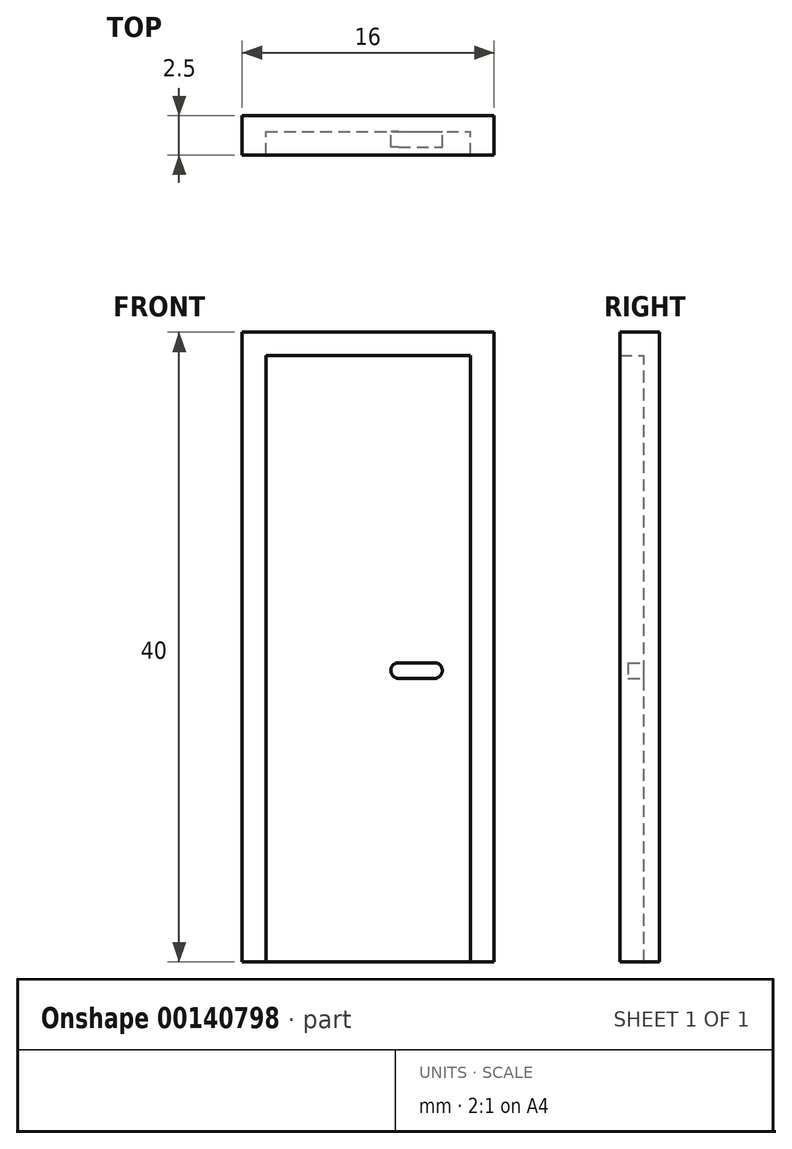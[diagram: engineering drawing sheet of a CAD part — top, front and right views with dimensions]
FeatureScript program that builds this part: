
annotation { "Feature Type Name" : "Feature", "Feature Type Description" : "" }
export const myFeature = defineFeature(function(context is Context, id is Id, definition is map)
    precondition{}
    {
        {
            var Q0;
            Q0=qCreatedBy(makeId("Front.planeOp"),FACE);
            var sketch = newSketch(context, id + "F0", { "sketchPlane" : qUnion([Q0])});
            skLineSegment(sketch, "E0.bottom", {"start": v(-11.07, 0) * mm, "end": v(4.93, 0) * mm});
            skLineSegment(sketch, "E0.top", {"start": v(-11.07, 40) * mm, "end": v(4.93, 40) * mm});
            skLineSegment(sketch, "E0.left", {"start": v(-11.07, 0) * mm, "end": v(-11.07, 40) * mm});
            skLineSegment(sketch, "E0.right", {"start": v(4.93, 0) * mm, "end": v(4.93, 40) * mm});
            skLineSegment(sketch, "E1.0", {"start": v(3.43, 0) * mm, "end": v(3.43, 38.5) * mm});
            skLineSegment(sketch, "E1.1", {"start": v(-9.57, 38.5) * mm, "end": v(3.43, 38.5) * mm});
            skLineSegment(sketch, "E1.2", {"start": v(-9.57, 0) * mm, "end": v(-9.57, 38.5) * mm});
            skSolve(sketch);
        }
        {
            var Q0;
            Q0=makeQuery(id+"F0.imprint","IMPRINT",FACE,{"disambiguationData":[TD([[makeQuery(id+"F0.imprint","IMPRINT",EDGE,{"derivedFrom":sQuery(id+"F0.wireOp",EDGE,"E0.top")}),-1.0]])]});
            extrude(context, id + "F1", {"entities" : qUnion([Q0]), "depth" : 2.5 * mm});
        }
        {
            var Q0;
            {var subQ0=sQuery(id+"F0.wireOp",EDGE,"E1.0");Q0=makeQuery(id+"F0.imprint","IMPRINT",FACE,{"disambiguationData":[TD([[makeQuery(id+"F0.imprint","IMPRINT",EDGE,{"derivedFrom":subQ0}),1.0]])]});}
            extrude(context, id + "F2", {"entities" : qUnion([Q0]), "operationType" : NewBodyOperationType.ADD, "depth" : 1 * mm});
        }
        {
            var Q0;
            Q0=makeQuery(id+"F2.opExtrude","CAP_FACE",FACE,{"disambiguationData":[OSD([sQuery(id+"F0.wireOp",EDGE,"E0.bottom"),sQuery(id+"F0.wireOp",EDGE,"E1.0"),sQuery(id+"F0.wireOp",EDGE,"E1.1"),sQuery(id+"F0.wireOp",EDGE,"E1.2")])],"isStart":false});
            var sketch = newSketch(context, id + "F3", { "sketchPlane" : qUnion([Q0])});
            skLineSegment(sketch, "E2", {"start": v(-1.13, 19) * mm, "end": v(1.14, 19) * mm});
            skLineSegment(sketch, "E3.0", {"start": v(-1.13, 18) * mm, "end": v(1.14, 18) * mm});
            skArc(sketch, "E4", {"start": v(-1.13, 19) * mm, "mid": v(-1.63, 18.5) * mm, "end": v(-1.13, 18) * mm});
            skArc(sketch, "E5", {"start": v(1.14, 18) * mm, "mid": v(1.64, 18.5) * mm, "end": v(1.14, 19) * mm});
            skSolve(sketch);
        }
        {
            var Q0;
            Q0=makeQuery(id+"F3.imprint","IMPRINT",FACE,{"disambiguationData":[TD([[makeQuery(id+"F3.imprint","IMPRINT",EDGE,{"derivedFrom":sQuery(id+"F3.wireOp",EDGE,"E2")}),-1.0]])]});
            extrude(context, id + "F4", {"entities" : qUnion([Q0]), "operationType" : NewBodyOperationType.ADD, "depth" : 1 * mm});
        }
    });
